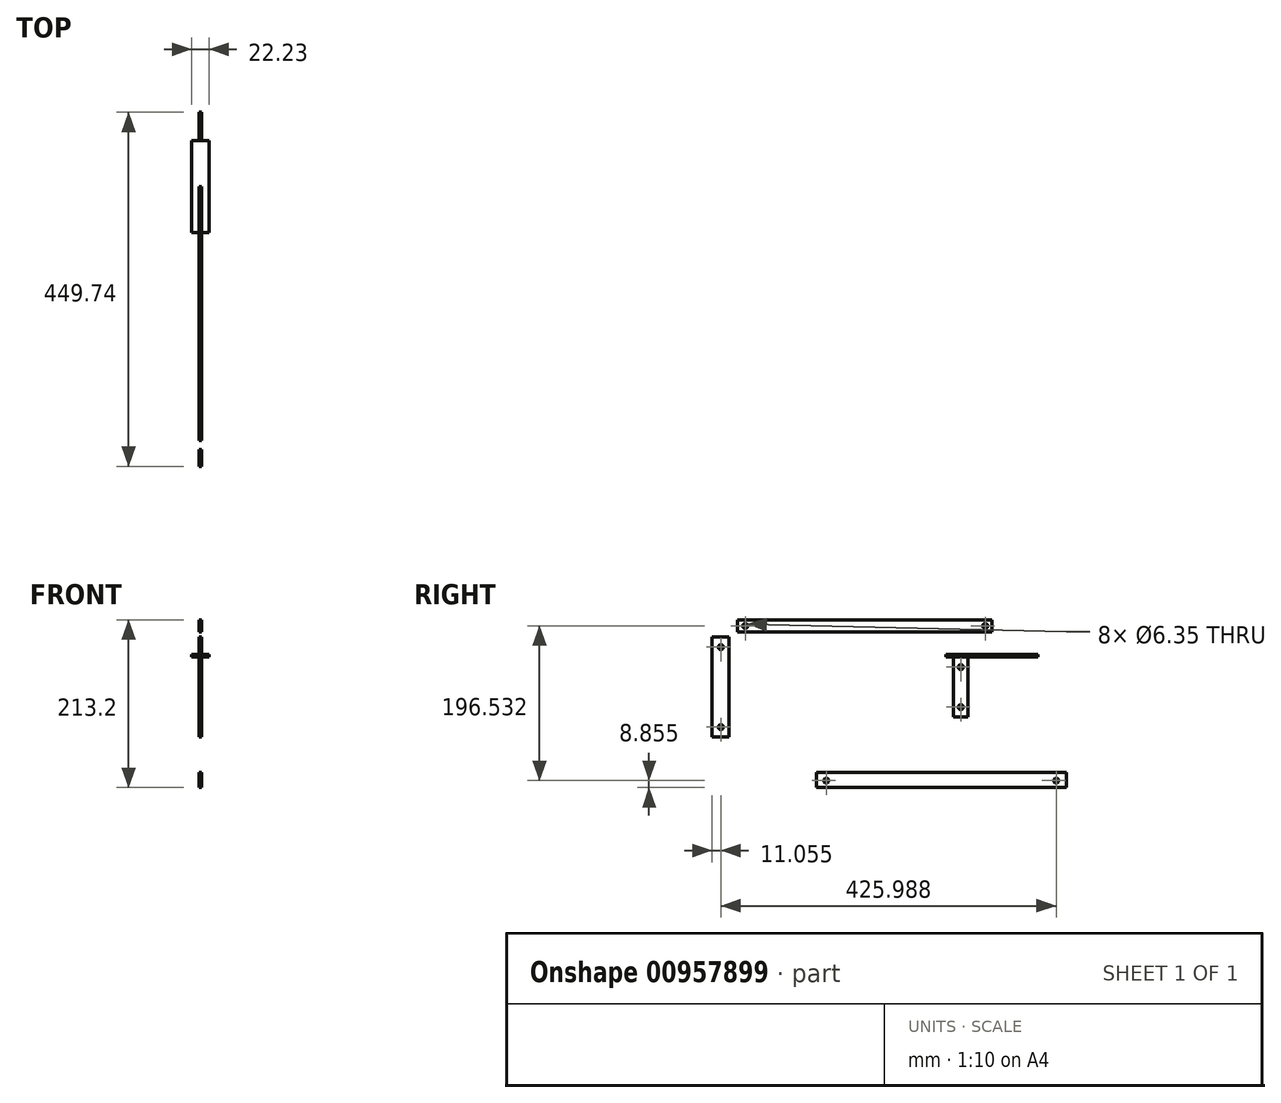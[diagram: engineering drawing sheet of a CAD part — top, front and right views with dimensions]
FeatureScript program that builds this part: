
annotation { "Feature Type Name" : "Feature", "Feature Type Description" : "" }
export const myFeature = defineFeature(function(context is Context, id is Id, definition is map)
    precondition{}
    {
        {
            var Q0;
            Q0=qCreatedBy(makeId("Right.planeOp"),FACE);
            var sketch = newSketch(context, id + "F0", { "sketchPlane" : qUnion([Q0])});
            skLineSegment(sketch, "E0", {"start": v(-154.9, 78.12) * mm, "end": v(-154.9, -54.86) * mm, "construction": true});
            skLineSegment(sketch, "E1", {"start": v(149.9, 78.12) * mm, "end": v(149.9, -45.9) * mm, "construction": true});
            skLineSegment(sketch, "E2", {"start": v(-164.15, 68.22) * mm, "end": v(-144.6, 68.22) * mm, "construction": true});
            skLineSegment(sketch, "E3", {"start": v(-170.94, -33.38) * mm, "end": v(-137.41, -33.38) * mm, "construction": true});
            skLineSegment(sketch, "E4", {"start": v(133.62, 42.82) * mm, "end": v(166.95, 42.82) * mm, "construction": true});
            skLineSegment(sketch, "E5", {"start": v(129.23, -7.98) * mm, "end": v(169.54, -7.98) * mm, "construction": true});
            skCircle(sketch, "E6", {"center": v(-154.9, 68.22) * mm, "radius": 3.18 * mm});
            skCircle(sketch, "E7", {"center": v(-154.9, -33.38) * mm, "radius": 3.18 * mm});
            skCircle(sketch, "E8", {"center": v(149.9, -7.98) * mm, "radius": 3.18 * mm});
            skCircle(sketch, "E9", {"center": v(149.9, 42.82) * mm, "radius": 3.18 * mm});
            skLineSegment(sketch, "E10", {"start": v(-166.55, 17.42) * mm, "end": v(177.33, 17.42) * mm, "construction": true});
            skLineSegment(sketch, "E11.bottom", {"start": v(-165.95, 80.92) * mm, "end": v(-144.8, 80.92) * mm});
            skLineSegment(sketch, "E11.top", {"start": v(-165.95, -46.08) * mm, "end": v(-144.8, -46.08) * mm});
            skLineSegment(sketch, "E11.left", {"start": v(-165.95, 80.92) * mm, "end": v(-165.95, -46.08) * mm});
            skLineSegment(sketch, "E11.right", {"start": v(-144.8, 80.92) * mm, "end": v(-144.8, -46.08) * mm});
            skLineSegment(sketch, "E12.bottom", {"start": v(140.6, 55.52) * mm, "end": v(159.16, 55.52) * mm});
            skLineSegment(sketch, "E12.top", {"start": v(140.6, -20.68) * mm, "end": v(159.16, -20.68) * mm});
            skLineSegment(sketch, "E12.left", {"start": v(140.6, 55.52) * mm, "end": v(140.6, -20.68) * mm});
            skLineSegment(sketch, "E12.right", {"start": v(159.16, 55.52) * mm, "end": v(159.16, -20.68) * mm});
            skSolve(sketch);
        }
        {
            var Q0;
            Q0 = qSketchRegion(id + "F0", true);
            extrude(context, id + "F1", {"entities" : qUnion([Q0]), "depth" : 3.17 * mm, "offsetDistance" : 25.4 * mm});
        }
        {
            var Q0;
            Q0=qCreatedBy(makeId("Right.planeOp"),FACE);
            var sketch = newSketch(context, id + "F2", { "sketchPlane" : qUnion([Q0])});
            skLineSegment(sketch, "E13", {"start": v(-67.32, 95) * mm, "end": v(191.7, 95) * mm, "construction": true});
            skLineSegment(sketch, "E14", {"start": v(-123.9, 101.12) * mm, "end": v(-123.9, 89.2) * mm, "construction": true});
            skLineSegment(sketch, "E15", {"start": v(180.9, 101.6) * mm, "end": v(180.9, 89.84) * mm, "construction": true});
            skCircle(sketch, "E16", {"center": v(-123.9, 95.16) * mm, "radius": 3.18 * mm});
            skCircle(sketch, "E17", {"center": v(180.9, 95) * mm, "radius": 3.18 * mm});
            skLineSegment(sketch, "E18.bottom", {"start": v(-133.5, 102.97) * mm, "end": v(189.51, 102.97) * mm});
            skLineSegment(sketch, "E18.top", {"start": v(-133.5, 87.3) * mm, "end": v(189.51, 87.3) * mm});
            skLineSegment(sketch, "E18.left", {"start": v(-133.5, 102.97) * mm, "end": v(-133.5, 87.3) * mm});
            skLineSegment(sketch, "E18.right", {"start": v(189.51, 102.97) * mm, "end": v(189.51, 87.3) * mm});
            skSolve(sketch);
        }
        {
            var Q0;
            Q0 = qSketchRegion(id + "F2", true);
            extrude(context, id + "F3", {"entities" : qUnion([Q0]), "depth" : 3.17 * mm, "offsetDistance" : 25.4 * mm});
        }
        {
            var Q0;
            Q0=qCreatedBy(makeId("Right.planeOp"),FACE);
            var sketch = newSketch(context, id + "F4", { "sketchPlane" : qUnion([Q0])});
            skLineSegment(sketch, "E19", {"start": v(-33.7, -101.37) * mm, "end": v(283.8, -101.37) * mm, "construction": true});
            skCircle(sketch, "E20", {"center": v(-21, -101.37) * mm, "radius": 3.18 * mm});
            skCircle(sketch, "E21", {"center": v(271.1, -101.37) * mm, "radius": 3.18 * mm});
            skLineSegment(sketch, "E22.bottom", {"start": v(-33.7, -90.94) * mm, "end": v(283.8, -90.94) * mm});
            skLineSegment(sketch, "E22.top", {"start": v(-33.7, -110.23) * mm, "end": v(283.8, -110.23) * mm});
            skLineSegment(sketch, "E22.left", {"start": v(-33.7, -90.94) * mm, "end": v(-33.7, -110.23) * mm});
            skLineSegment(sketch, "E22.right", {"start": v(283.8, -90.94) * mm, "end": v(283.8, -110.23) * mm});
            skSolve(sketch);
        }
        {
            var Q0;
            Q0 = qSketchRegion(id + "F4", true);
            extrude(context, id + "F5", {"entities" : qUnion([Q0]), "depth" : 3.17 * mm, "offsetDistance" : 25.4 * mm});
        }
        {
            var Q0;
            Q0=makeQuery(id+"F1.opExtrude","CAP_FACE",FACE,{"disambiguationData":[OSD([sQuery(id+"F0.wireOp",EDGE,"E8"),sQuery(id+"F0.wireOp",EDGE,"E9"),sQuery(id+"F0.wireOp",EDGE,"E12.bottom"),sQuery(id+"F0.wireOp",EDGE,"E12.top"),sQuery(id+"F0.wireOp",EDGE,"E12.left"),sQuery(id+"F0.wireOp",EDGE,"E12.right")])],"isStart":false});
            var sketch = newSketch(context, id + "F6", { "sketchPlane" : qUnion([Q0])});
            skLineSegment(sketch, "E23.bottom", {"start": v(131.08, 55.52) * mm, "end": v(248.06, 55.52) * mm});
            skLineSegment(sketch, "E23.top", {"start": v(131.08, 58.7) * mm, "end": v(248.06, 58.7) * mm});
            skLineSegment(sketch, "E23.left", {"start": v(131.08, 55.52) * mm, "end": v(131.08, 58.7) * mm});
            skLineSegment(sketch, "E23.right", {"start": v(248.06, 55.52) * mm, "end": v(248.06, 58.7) * mm});
            skSolve(sketch);
        }
        {
            var Q0;
            Q0 = qSketchRegion(id + "F6", true);
            extrude(context, id + "F7", {"entities" : qUnion([Q0]), "operationType" : NewBodyOperationType.ADD, "depth" : 9.52 * mm, "offsetDistance" : 25.4 * mm, "hasSecondDirection" : true, "secondDirectionOppositeDirection" : true, "secondDirectionDepth" : 12.7 * mm});
        }
    });
